# Revit family: SinkMixer-Countertop-MaestroPullOut-Vitra-MasterlineSeries-A42146
name_source: partatom
category: Plumbing Fixtures
revit_build: Autodesk Revit 2017 (Build: 20160225_1515(x64)
units: mm (PartAtom-declared; Revit-internal decimal feet)

## family parameters
Cut with Voids When Loaded = No
Host = Face
OmniClass Number = 23.45.55.17
OmniClass Title = Mixing Faucets
Part Type = Normal
Room Calculation Point = No
Round Connector Dimension = Use Diameter
Shared = Yes

## types (4) — shared parameters
BIMobject category = Sink Mixer
CW Connection = Yes
Coating Material = Chrome
Color = Chrome
Default Elevation = 850 mm  [stored 2.78871 ft]
Description = Masterline Maestro Pull-Out
Design country = Turkey
Flow Rate(L/min. - 3 bar) = 8 L/min.
HW Connection = Yes
Hot Water Supply (max.) = 80 °C
Hot Water temperature, factory set to = 38 °C
IFC Classification = Sanitary Terminal
Main Material = Brass
Manufacturer = Vitra
Manufacturer name = Vitra
Masterformat 2014 Code = 22 40 00
Masterformat 2014 Description = Plumbing Fixtures
Min. flow pressure of = 0.5 bar
Mounting type = Countertop
NBS Referans Code = 45-35-70/345
NBS Referans Description = Water supply fittings for sinks
Nominal Depth (mm) = 215 mm
Nominal Height (mm) = 349 mm  [stored 1.14501 ft]
Nominal Width (mm) = 135 mm
Number Of Connections = 2
OmniClass Code = 23.45.55.17
OmniClass Description = Mixing Faucets
Product Properties = Water Saving
Product Type = Sink Mixer
Product certification = https://www.vitraglobal.com
Product family = Masterline
Product group = Maestro Pull-Out - Masterline
Range of Hot Water Supply = 5 - 65 °C
Range of flow pressure = 1 - 5 bar
Test Pressure = 16 bar
URL = https://vitraglobal.com
Uniclass 1.4 Code = L725111
Uniclass 1.4 Description = Sink Mixer
Uniclass 2.0 Code = Pr_40_30_96_47
Uniclass 2.0 Description = Kitchen Taps
Uniclass 2015 Code = Pr_40_20_87_84
Uniclass 2015 Name = Sink taps
Uniformat II Code = 22 40 00
Uniformat II Description = Plumbing Fixture
Vent Connection = No
Warranty Period (Year) = 10 Years
Waste Connection = No
Weight Net (kg) = 2.83
Youtube = https://www.youtube.com

## per-type parameters (varying)
| type | Article No. (default) | Brand | Connection Diameter (mm) | Model | Product SKU | Product url | Technical description |
| SinkMixer-Countertop-MaestroPullOut-Vitra-MasterlineSeries-A42146 | A42146 | Artema | 10 mm  [stored 0.0328084 ft] | A42146 | A42146 | https://www.vitra.com.tr | https://www.vitra.com.tr |
| SinkMixer-Countertop-MaestroPullOut-Vitra-MasterlineSeries-A42146EKM | A42146EKM | VitrA | 10 mm  [stored 0.0328084 ft] | A42146EKM | A42146EKM | https://www.vitra-bad.fr | http://cdn.vitra.com.tr |
| SinkMixer-Countertop-MaestroPullOut-Vitra-MasterlineSeries-A42146EXP | A42146EXP | VitrA | 10 mm  [stored 0.0328084 ft] | A42146EXP | A42146EXP | https://vitraglobal.com | https://vitraglobal.com |
| SinkMixer-Countertop-MaestroPullOut-Vitra-MasterlineSeries-A42146IND | A42146IND | VitrA | 15 mm  [stored 0.0492126 ft] | A42146IND | A42146IND | https://www.vitra-india.com | https://www.vitra-india.com |

note: [stored X ft] marks values corroborated as IEEE doubles in the binary element streams (Revit-internal decimal feet)

## geometry (parser evidence)
native form markers: Sweep x2
no freeform markers — native parametric forms only
